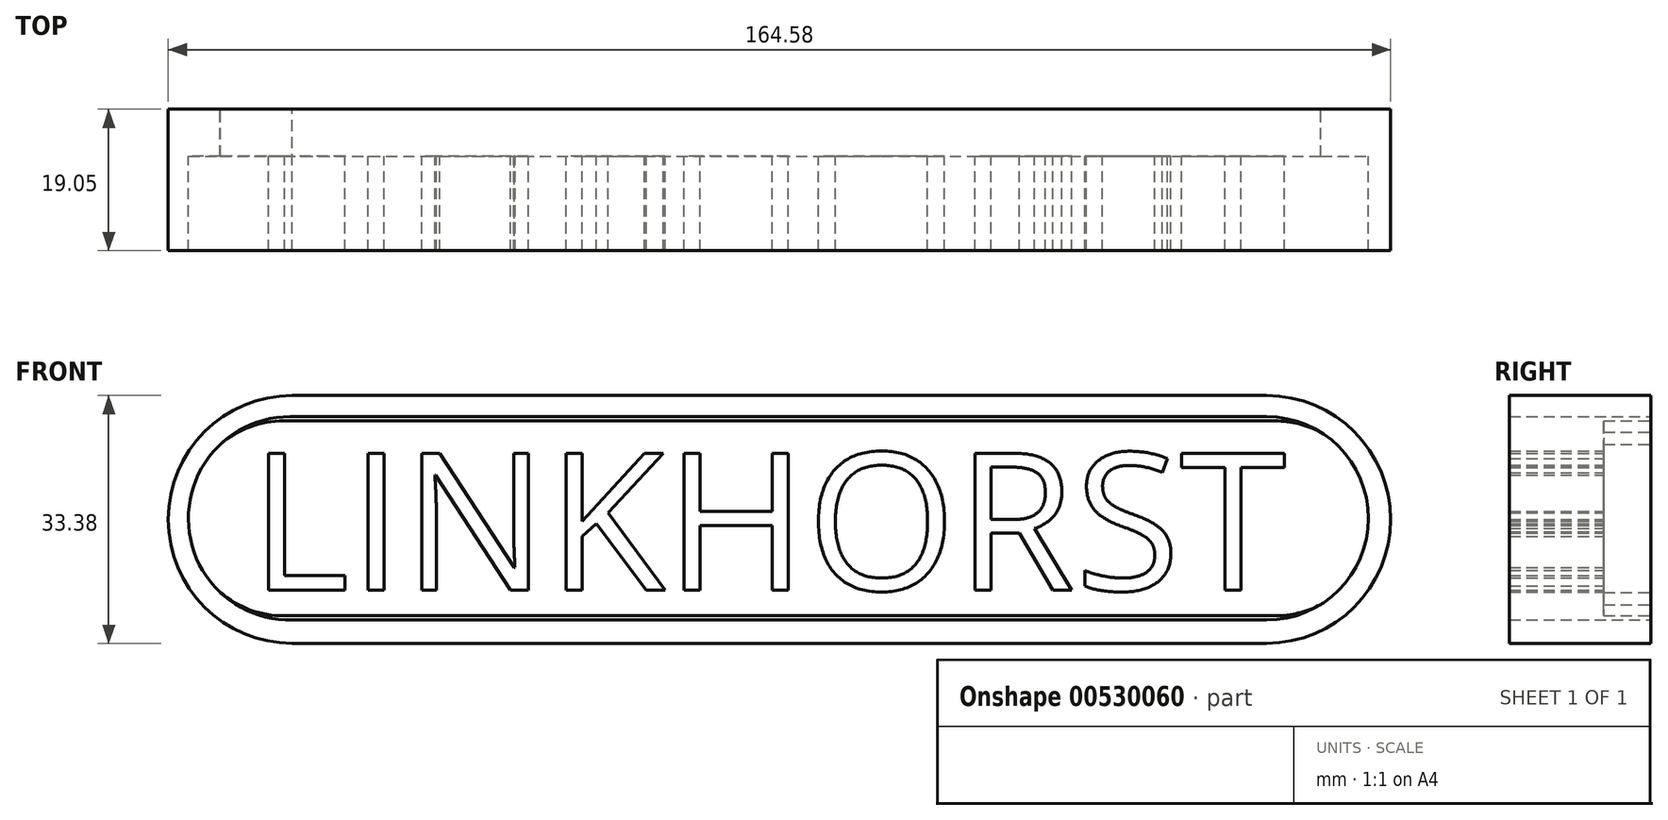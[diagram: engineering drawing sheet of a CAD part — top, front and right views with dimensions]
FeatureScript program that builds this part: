
annotation { "Feature Type Name" : "Feature", "Feature Type Description" : "" }
export const myFeature = defineFeature(function(context is Context, id is Id, definition is map)
    precondition{}
    {
        {
            var Q0;
            Q0=qCreatedBy(makeId("Front.planeOp"),FACE);
            var sketch = newSketch(context, id + "F0", { "sketchPlane" : qUnion([Q0])});
            skLineSegment(sketch, "E0", {"start": v(65.6, -16.69) * mm, "end": v(-65.6, -16.69) * mm});
            skLineSegment(sketch, "E1.MirrorCS", {"start": v(65.6, 16.69) * mm, "end": v(-65.6, 16.69) * mm});
            skArc(sketch, "E2", {"start": v(-65.6, 16.69) * mm, "mid": v(-82.3, 0) * mm, "end": v(-65.6, -16.69) * mm});
            skArc(sketch, "E3", {"start": v(65.6, 16.69) * mm, "mid": v(82.3, 0) * mm, "end": v(65.6, -16.69) * mm});
            skLineSegment(sketch, "E4", {"start": v(-65.9, 13.83) * mm, "end": v(65.6, 13.83) * mm});
            skLineSegment(sketch, "E5", {"start": v(-65.6, -13.55) * mm, "end": v(65.6, -13.55) * mm});
            skArc(sketch, "E6", {"start": v(-65.9, 13.83) * mm, "mid": v(-79.58, 0) * mm, "end": v(-65.6, -13.55) * mm});
            skArc(sketch, "E7", {"start": v(65.6, 13.83) * mm, "mid": v(79.3, 0.14) * mm, "end": v(65.6, -13.55) * mm});
            skSolve(sketch);
        }
        {
            var Q0;
            Q0=qSketchRegion(id+"F0",true);
            extrude(context, id + "F1", {"entities" : qUnion([Q0]), "depth" : 19.05 * mm});
        }
        {
            var Q0;
            Q0=qCreatedBy(makeId("Front.planeOp"),FACE);
            var sketch = newSketch(context, id + "F2", { "sketchPlane" : qUnion([Q0])});
            skLineSegment(sketch, "E8.bottom", {"start": v(-66.75, 13.26) * mm, "end": v(66.75, 13.26) * mm});
            skLineSegment(sketch, "E8.top", {"start": v(-66.75, -12.98) * mm, "end": v(66.75, -12.98) * mm});
            skLineSegment(sketch, "E8.left", {"start": v(-66.75, 13.26) * mm, "end": v(-66.75, -12.98) * mm});
            skLineSegment(sketch, "E8.right", {"start": v(66.75, 13.26) * mm, "end": v(66.75, -12.98) * mm});
            skArc(sketch, "E9", {"start": v(-66.75, 13.26) * mm, "mid": v(-79.87, 0.14) * mm, "end": v(-66.75, -12.98) * mm});
            skArc(sketch, "E10.MirrorCS", {"start": v(-66.75, -13.26) * mm, "mid": v(-79.87, -0.14) * mm, "end": v(-66.75, 12.98) * mm});
            skArc(sketch, "E11", {"start": v(66.75, -12.98) * mm, "mid": v(79.87, 0.14) * mm, "end": v(66.75, 13.26) * mm});
            skSolve(sketch);
        }
        {
            var Q0;
            Q0=qSketchRegion(id+"F2",true);
            extrude(context, id + "F3", {"entities" : qUnion([Q0]), "operationType" : NewBodyOperationType.ADD, "depth" : 6.35 * mm});
        }
        {
            var Q0;
            Q0=makeQuery(id+"F3.opExtrude","CAP_FACE",FACE,{"disambiguationData":[OSD([sQuery(id+"F2.wireOp",EDGE,"E8.bottom"),sQuery(id+"F2.wireOp",EDGE,"E8.top"),sQuery(id+"F2.wireOp",EDGE,"E9"),sQuery(id+"F2.wireOp",EDGE,"E11")])],"isStart":false});
            var sketch = newSketch(context, id + "F4", { "sketchPlane" : qUnion([Q0])});
            skText(sketch, "E12", { "text": "LINKHORST", "fontName": "OpenSans-Regular.ttf"});
            const initialGuessF4  = {"E12": [-0.07132, -0.00952, 1, 0, 0.0186]};
            skSetInitialGuess(sketch, initialGuessF4);
            skSolve(sketch);
        }
        {
            var Q0;
            Q0=qSketchRegion(id+"F4",true);
            extrude(context, id + "F5", {"entities" : qUnion([Q0]), "operationType" : NewBodyOperationType.ADD, "depth" : 12.7 * mm});
        }
    });
